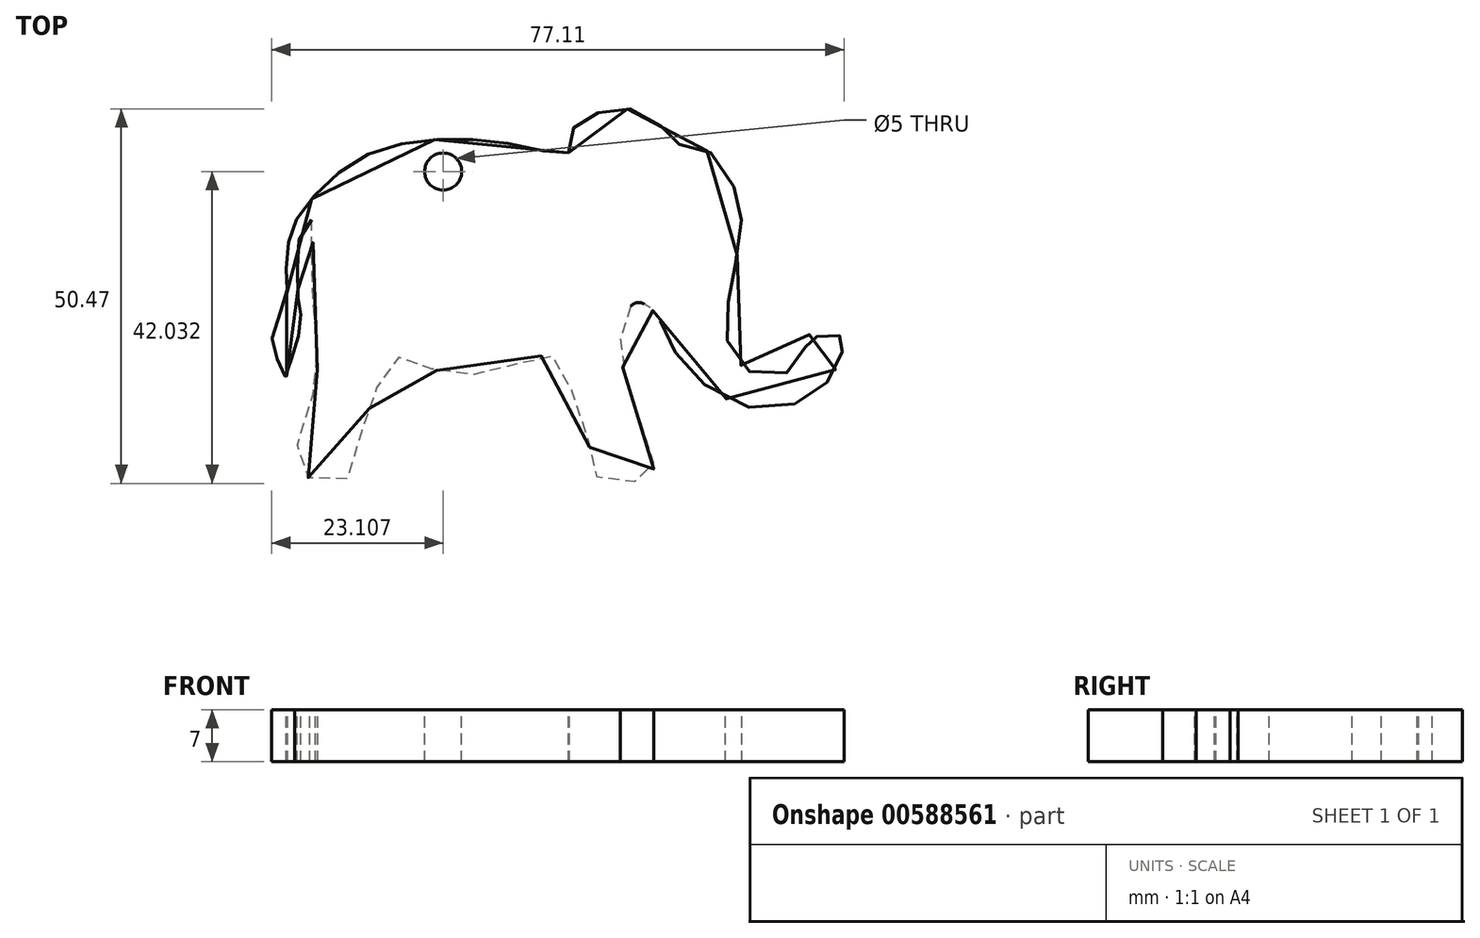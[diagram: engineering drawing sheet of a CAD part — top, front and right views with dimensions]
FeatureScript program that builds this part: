
annotation { "Feature Type Name" : "Feature", "Feature Type Description" : "" }
export const myFeature = defineFeature(function(context is Context, id is Id, definition is map)
    precondition{}
    {
        {
            var Q0;
            Q0=qCreatedBy(makeId("Top.planeOp"),FACE);
            var sketch = newSketch(context, id + "F0", { "sketchPlane" : qUnion([Q0])});
            skFitSpline(sketch, "E0", {"points": [v(-38.04, 58.58) * mm, v(-38.04, 60.23) * mm, v(-36.76, 62.6) * mm, v(-34.48, 63.88) * mm, v(-31.74, 64.34) * mm, v(-27.8, 64.16) * mm, v(-25.07, 61.41) * mm, v(-23.97, 60.04) * mm, v(-20.5, 59.22) * mm, v(-18.03, 57.85) * mm, v(-15.2, 52.55) * mm, v(-14.74, 49.35) * mm, v(-15.65, 42.96) * mm, v(-16.48, 38.66) * mm, v(-16.84, 34.1) * mm, v(-14.56, 29.7) * mm, v(-10.9, 28.61) * mm, v(-6.8, 30.07) * mm, v(-6.06, 33.27) * mm, v(-5.7, 34.1) * mm, v(-4.14, 33.64) * mm, v(-2.5, 33.27) * mm, v(-1.13, 34.28) * mm, v(-0.94, 33.46) * mm, v(-1.68, 30.26) * mm, v(-3.78, 27.06) * mm, v(-8.16, 24.6) * mm, v(-14.83, 24.6) * mm, v(-21.32, 28.8) * mm, v(-24.24, 32.72) * mm, v(-25.8, 36.1) * mm, v(-27.62, 38.12) * mm, v(-29.18, 38.3) * mm, v(-30.55, 36.29) * mm, v(-31.1, 33.36) * mm, v(-30.55, 28.8) * mm, v(-29, 23.86) * mm, v(-27.17, 18.93) * mm, v(-26.62, 16.73) * mm, v(-26.9, 15.04) * mm, v(-30.11, 14.14) * mm, v(-33.77, 14.47) * mm, v(-34.84, 17.1) * mm, v(-36.03, 22.22) * mm, v(-38.04, 27.7) * mm, v(-39.69, 30.9) * mm, v(-42.33, 31.08) * mm, v(-45.26, 29.98) * mm, v(-50.74, 28.7) * mm, v(-54.67, 28.98) * mm, v(-59.1, 30.46) * mm, v(-60.88, 31.08) * mm, v(-62.9, 29.25) * mm, v(-64.72, 24.5) * mm, v(-66.55, 18.93) * mm, v(-68.1, 14.45) * mm, v(-71.75, 14.59) * mm, v(-74.72, 15.69) * mm, v(-73.95, 21.4) * mm, v(-72.21, 27.06) * mm, v(-71.85, 31.9) * mm, v(-72.4, 38.39) * mm, v(-72.85, 44.42) * mm, v(-72.15, 48.74) * mm, v(-72.49, 49.63) * mm, v(-74.2, 47.4) * mm, v(-74.59, 42.68) * mm, v(-74.4, 38.12) * mm, v(-74.13, 36.84) * mm, v(-74.4, 34) * mm, v(-75.41, 30.62) * mm, v(-76.14, 28.43) * mm, v(-76.8, 29.95) * mm, v(-78, 32.27) * mm, v(-77.11, 36.52) * mm, v(-75.98, 39.77) * mm, v(-76.05, 42.23) * mm, v(-75.8, 46.4) * mm, v(-74.59, 49.81) * mm, v(-70.93, 54.2) * mm, v(-65.09, 58.4) * mm, v(-57.87, 60.23) * mm, v(-50.2, 60.32) * mm, v(-42.6, 59.13) * mm, v(-38.04, 58.58) * mm]});
            skSolve(sketch);
        }
        {
            var Q0;
            Q0=makeQuery(id+"F0.imprint","IMPRINT",FACE,{"disambiguationData":[TD([[makeQuery(id+"F0.imprint","IMPRINT",EDGE,{"derivedFrom":sQuery(id+"F0.wireOp",EDGE,"E0")}),-1.0]])]});
            extrude(context, id + "F1", {"entities" : qUnion([Q0]), "oppositeDirection" : true, "depth" : 7 * mm, "offsetDistance" : 25 * mm});
        }
        {
            var Q0;
            Q0=makeQuery(id+"F1.opExtrude","CAP_FACE",FACE,{"disambiguationData":[OSD([sQuery(id+"F0.wireOp",EDGE,"E0")])],"isStart":true});
            var sketch = newSketch(context, id + "F2", { "sketchPlane" : qUnion([Q0])});
            skCircle(sketch, "E1", {"center": v(-54.94, 56.07) * mm, "radius": 2.5 * mm});
            skSolve(sketch);
        }
        {
            var Q0;
            Q0=makeQuery(id+"F2.imprint","IMPRINT",FACE,{"disambiguationData":[TD([[makeQuery(id+"F2.imprint","IMPRINT",EDGE,{"derivedFrom":sQuery(id+"F2.wireOp",EDGE,"E1")}),1.0]])]});
            extrude(context, id + "F3", {"entities" : qUnion([Q0]), "operationType" : NewBodyOperationType.REMOVE, "oppositeDirection" : true, "depth" : 7 * mm, "offsetDistance" : 25 * mm});
        }
    });
